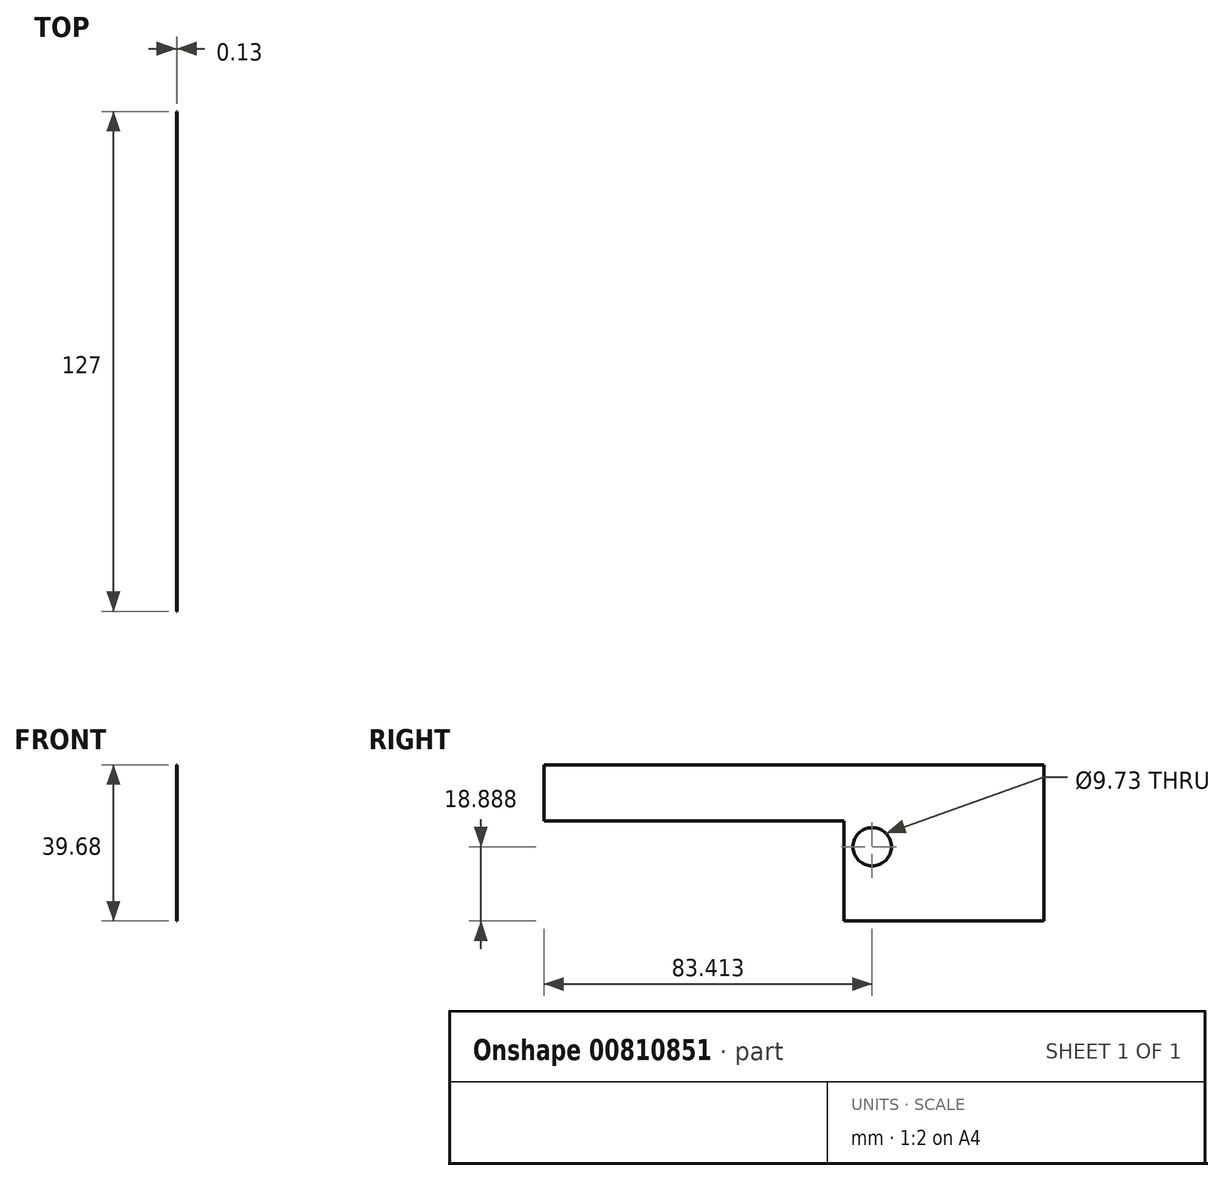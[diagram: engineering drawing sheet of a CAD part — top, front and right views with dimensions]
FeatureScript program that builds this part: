
annotation { "Feature Type Name" : "Feature", "Feature Type Description" : "" }
export const myFeature = defineFeature(function(context is Context, id is Id, definition is map)
    precondition{}
    {
        {
            assignVariable(context, id + "F0", {"name" : "x", "anyValue" : .125});
        }
        {
            var Q0;
            Q0=qCreatedBy(makeId("Right.planeOp"),FACE);
            var sketch = newSketch(context, id + "F1", { "sketchPlane" : qUnion([Q0])});
            skLineSegment(sketch, "E0.bottom", {"start": v(-63.5, 7.14) * mm, "end": v(63.5, 7.14) * mm});
            skLineSegment(sketch, "E0.top", {"start": v(-63.5, -7.14) * mm, "end": v(63.5, -7.14) * mm});
            skLineSegment(sketch, "E0.left", {"start": v(-63.5, 7.14) * mm, "end": v(-63.5, -7.14) * mm});
            skLineSegment(sketch, "E0.right", {"start": v(63.5, 7.14) * mm, "end": v(63.5, -7.14) * mm});
            skPoint(sketch, "E0.middle", {"position": v(0, 0) * mm});
            skLineSegment(sketch, "E1.bottom", {"start": v(63.5, -7.14) * mm, "end": v(12.7, -7.14) * mm});
            skLineSegment(sketch, "E1.top", {"start": v(63.5, -32.54) * mm, "end": v(12.7, -32.54) * mm});
            skLineSegment(sketch, "E1.left", {"start": v(63.5, -7.14) * mm, "end": v(63.5, -32.54) * mm});
            skLineSegment(sketch, "E1.right", {"start": v(12.7, -7.14) * mm, "end": v(12.7, -32.54) * mm});
            skCircle(sketch, "E2", {"center": v(19.91, -13.65) * mm, "radius": 4.87 * mm});
            skSolve(sketch);
        }
        {
            var Q0;
            Q0=makeQuery(id+"F1.imprint","IMPRINT",FACE,{"disambiguationData":[TD([[makeQuery(id+"F1.imprint","IMPRINT",EDGE,{"derivedFrom":sQuery(id+"F1.wireOp",EDGE,"E0.bottom")}),-1.0]])]});
            var Q1;
            Q1=makeQuery(id+"F1.imprint","IMPRINT",FACE,{"disambiguationData":[TD([[makeQuery(id+"F1.imprint","IMPRINT",EDGE,{"derivedFrom":sQuery(id+"F1.wireOp",EDGE,"E1.top")}),-1.0]])]});
            extrude(context, id + "F2", {"entities" : qUnion([Q0, Q1]), "oppositeDirection" : true, "depth" : (getVariable(context, 'x')) * mm, "offsetDistance" : 25.4 * mm});
        }
    });
